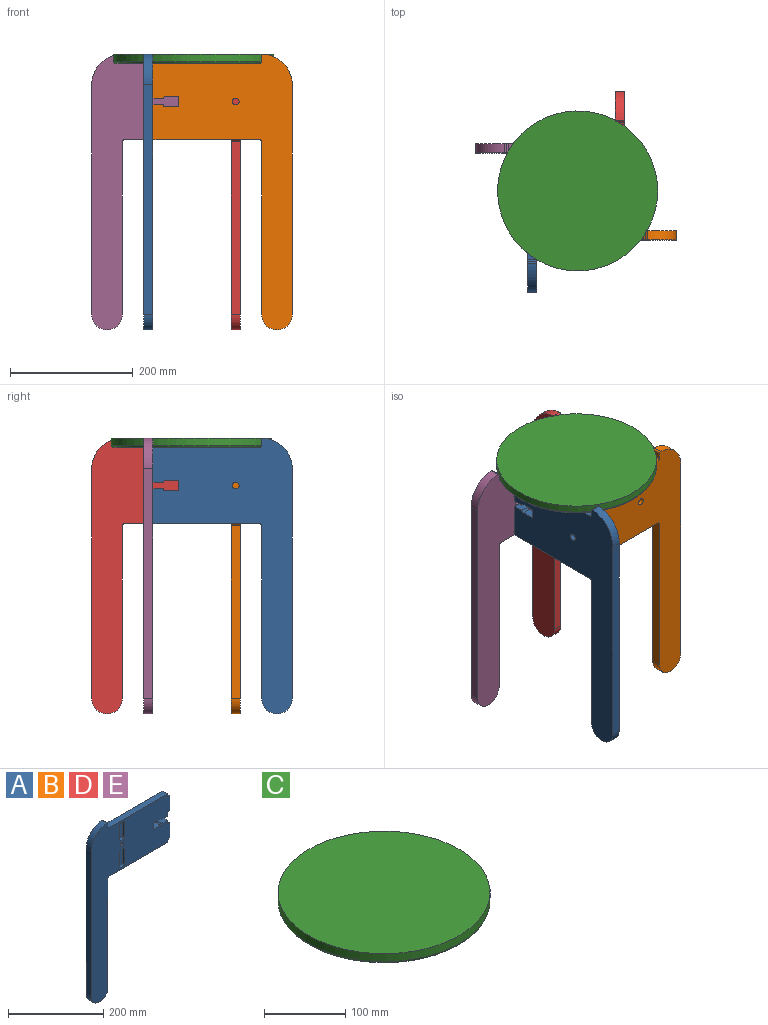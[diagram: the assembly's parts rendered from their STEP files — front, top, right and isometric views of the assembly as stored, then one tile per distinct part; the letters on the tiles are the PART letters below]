
ASSEMBLY  parts=5 mates=10
PART A: 54 faces, bbox 234.3x15x449.9 mm
  f0: plane 449.9x234.25mm, normal (0,-1,0), area 42400.1mm2, adj f1,f3,f4,f5,f6,f7,f8,f9
  f1: plane 15x7mm, normal (1,0,0), area 105mm2, adj f0,f2,f25,f45
  f2: plane 449.9x234.25mm, normal (0,1,0), area 43707.6mm2, adj f1,f3,f4,f5,f6,f7,f8,f9
  f3: plane 15x7mm, normal (1,0,0), area 105mm2, adj f0,f2,f24,f50
  f4: plane 15x5mm, normal (1,0,0), area 75mm2, adj f0,f2,f17,f23
  f5: plane 15x5mm, normal (1,0,0), area 75mm2, adj f0,f2,f8,f26
  f6: plane 39x15mm, normal (1,0,0), area 585mm2, adj f0,f2,f19,f21
  f7: plane 39x15mm, normal (1,0,0), area 585mm2, adj f0,f2,f20,f22
  f8: plane 174.25x15mm, normal (0,0,1), area 2613.7mm2, adj f0,f2,f5,f9
  f9: cylinder r=3mm len=15mm, axis (0,1,0), area 70.7mm2, adj f0,f2,f8,f10
  f10: plane 15x8.9mm, normal (1,0,0), area 133.6mm2, adj f0,f2,f9,f11
  f11: cylinder r=3mm len=15mm, axis (0,1,0), area 73.6mm2, adj f0,f2,f10,f12
  f12: cylinder r=50mm len=49.9mm, axis (0,1,0), area 1130.2mm2, adj f0,f2,f11,f13
  f13: plane 375x15mm, normal (-1,0,0), area 5625mm2, adj f0,f2,f12,f14
  f14: cylinder r=25mm len=50mm, axis (0,1,0), area 1178.1mm2, adj f0,f2,f13,f15
  f15: plane 282x15mm, normal (1,0,0), area 4230mm2, adj f0,f2,f14,f16
  f16: cylinder r=3mm len=15mm, axis (0,1,0), area 70.7mm2, adj f0,f2,f15,f17
  f17: plane 174.25x15mm, normal (0,0,-1), area 2613.7mm2, adj f0,f2,f4,f16
  f18: cylinder r=5.5mm len=15mm, axis (0,1,0), area 518.4mm2, adj f0,f2
  f19: plane 15x4mm, normal (0,0,1), area 60mm2, adj f0,f2,f6,f26
  f20: plane 15x4mm, normal (0,0,-1), area 60mm2, adj f0,f2,f7,f23
  f21: plane 15x4mm, normal (0,0,-1), area 60mm2, adj f0,f2,f6,f25
  f22: plane 15x4mm, normal (0,0,1), area 60mm2, adj f0,f2,f7,f24
  f23: cylinder r=3mm len=15mm, axis (0,-1,0), area 70.7mm2, adj f0,f2,f4,f20
  f24: cylinder r=3mm len=15mm, axis (0,1,0), area 70.7mm2, adj f0,f2,f3,f22
  f25: cylinder r=3mm len=15mm, axis (0,-1,0), area 70.7mm2, adj f0,f1,f2,f21
  f26: cylinder r=3mm len=15mm, axis (0,-1,0), area 70.7mm2, adj f0,f2,f5,f19
  f27: plane 8.7x7mm, normal (0,0,-1), area 60.9mm2, adj f0,f28,f34,f35
  f28: cylinder r=3mm len=7mm, axis (0,-1,0), area 33mm2, adj f0,f27,f29,f35
  f29: plane 39x7mm, normal (1,0,0), area 273mm2, adj f0,f28,f30,f35
  f30: cylinder r=3mm len=7mm, axis (0,-1,0), area 33mm2, adj f0,f29,f31,f35
  f31: plane 8.7x7mm, normal (0,0,1), area 60.9mm2, adj f0,f30,f32,f35
  f32: cylinder r=3mm len=7mm, axis (0,-1,0), area 33mm2, adj f0,f31,f33,f35
  f33: plane 39x7mm, normal (-1,0,0), area 273mm2, adj f0,f32,f34,f35
  f34: cylinder r=3mm len=7mm, axis (0,-1,0), area 33mm2, adj f0,f27,f33,f35
  f35: plane 45x14.7mm, normal (0,-1,0), area 653.8mm2, adj f27,f28,f29,f30,f31,f32,f33,f34
  f36: plane 8.7x7mm, normal (0,0,-1), area 60.9mm2, adj f0,f37,f43,f44
  f37: cylinder r=3mm len=7mm, axis (0,-1,0), area 33mm2, adj f0,f36,f38,f44
  f38: plane 39x7mm, normal (1,0,0), area 273mm2, adj f0,f37,f39,f44
  f39: cylinder r=3mm len=7mm, axis (0,-1,0), area 33mm2, adj f0,f38,f40,f44
  f40: plane 8.7x7mm, normal (0,0,1), area 60.9mm2, adj f0,f39,f41,f44
  f41: cylinder r=3mm len=7mm, axis (0,-1,0), area 33mm2, adj f0,f40,f42,f44
  f42: plane 39x7mm, normal (-1,0,0), area 273mm2, adj f0,f41,f43,f44
  f43: cylinder r=3mm len=7mm, axis (0,-1,0), area 33mm2, adj f0,f36,f42,f44
  f44: plane 45x14.7mm, normal (0,-1,0), area 653.8mm2, adj f36,f37,f38,f39,f40,f41,f42,f43
  f45: plane 17x15mm, normal (0,0,-1), area 255mm2, adj f0,f1,f2,f46
  f46: cylinder r=3mm len=15mm, axis (0,-1,0), area 70.7mm2, adj f0,f2,f45,f47
  f47: plane 19x15mm, normal (0,0,-1), area 285mm2, adj f0,f2,f46,f51
  f48: plane 19x15mm, normal (0,0,1), area 285mm2, adj f0,f2,f49,f53
  f49: cylinder r=3mm len=15mm, axis (0,-1,0), area 70.7mm2, adj f0,f2,f48,f50
  f50: plane 17x15mm, normal (0,0,1), area 255mm2, adj f0,f2,f3,f49
  f51: cylinder r=3mm len=15mm, axis (0,-1,0), area 70.7mm2, adj f0,f2,f47,f52
  f52: plane 15x11mm, normal (1,0,0), area 165mm2, adj f0,f2,f51,f53
  f53: cylinder r=3mm len=15mm, axis (0,-1,0), area 70.7mm2, adj f0,f2,f48,f52
PART B: same geometry as A
PART C: 4 faces, bbox 282.5x282.5x15 mm
  f0: cylinder r=130.5mm len=261mm, axis (0,0,-1), area 9839.5mm2, adj f1,f3
  f1: plane 261x261mm, normal (0,0,1), area 53502.1mm2, adj f0
  f2: plane 255x255mm, normal (0,0,-1), area 51070.5mm2, adj f3
  f3: torus R=127.5mm, axis (0,0,1), area 3831.7mm2, adj f0,f2
PART D: same geometry as A
PART E: same geometry as A
PLACE A rot(axis=(0,0,1),90deg) t=(-32.76,-5.28,250.14)mm
PLACE B rot(axis=(0,0,1),180deg) t=(-17.76,-147.63,250.14)mm
PLACE C t=(48.62,-67.61,235.14)mm
PLACE D rot(axis=(0,0,-1),90deg) t=(124.59,-132.63,250.14)mm
PLACE E t=(109.59,9.72,250.14)mm fixed
MATE planar D.f8 <-> A.f8  axis (0,0,1) through (117.09,-45.51,235.14)mm
MATE planar D.f2 <-> B.f29  axis (1,0,0) through (124.59,11.87,98.14)mm
MATE planar B.f5 <-> A.f0  axis (-1,0,0) through (-17.76,-147.63,232.64)mm
MATE planar A.f3 <-> E.f0  axis (0,1,0) through (-25.26,-5.28,163.64)mm
MATE planar A.f29 <-> B.f2  axis (0,1,0) through (-21.26,-147.63,207.64)mm
MATE planar C.f0 <-> D.f8  axis (0,0,-1) through (48.62,-67.61,235.14)mm
MATE planar A.f2 <-> E.f29  axis (-1,0,0) through (-32.76,-149.78,98.14)mm
MATE planar D.f8 <-> B.f8  axis (0,0,1) through (117.09,-45.51,235.14)mm
MATE planar A.f8 <-> E.f8  axis (0,0,1) through (-25.26,-92.41,235.14)mm
MATE planar D.f3 <-> B.f0  axis (0,-1,0) through (117.09,-132.63,163.64)mm
